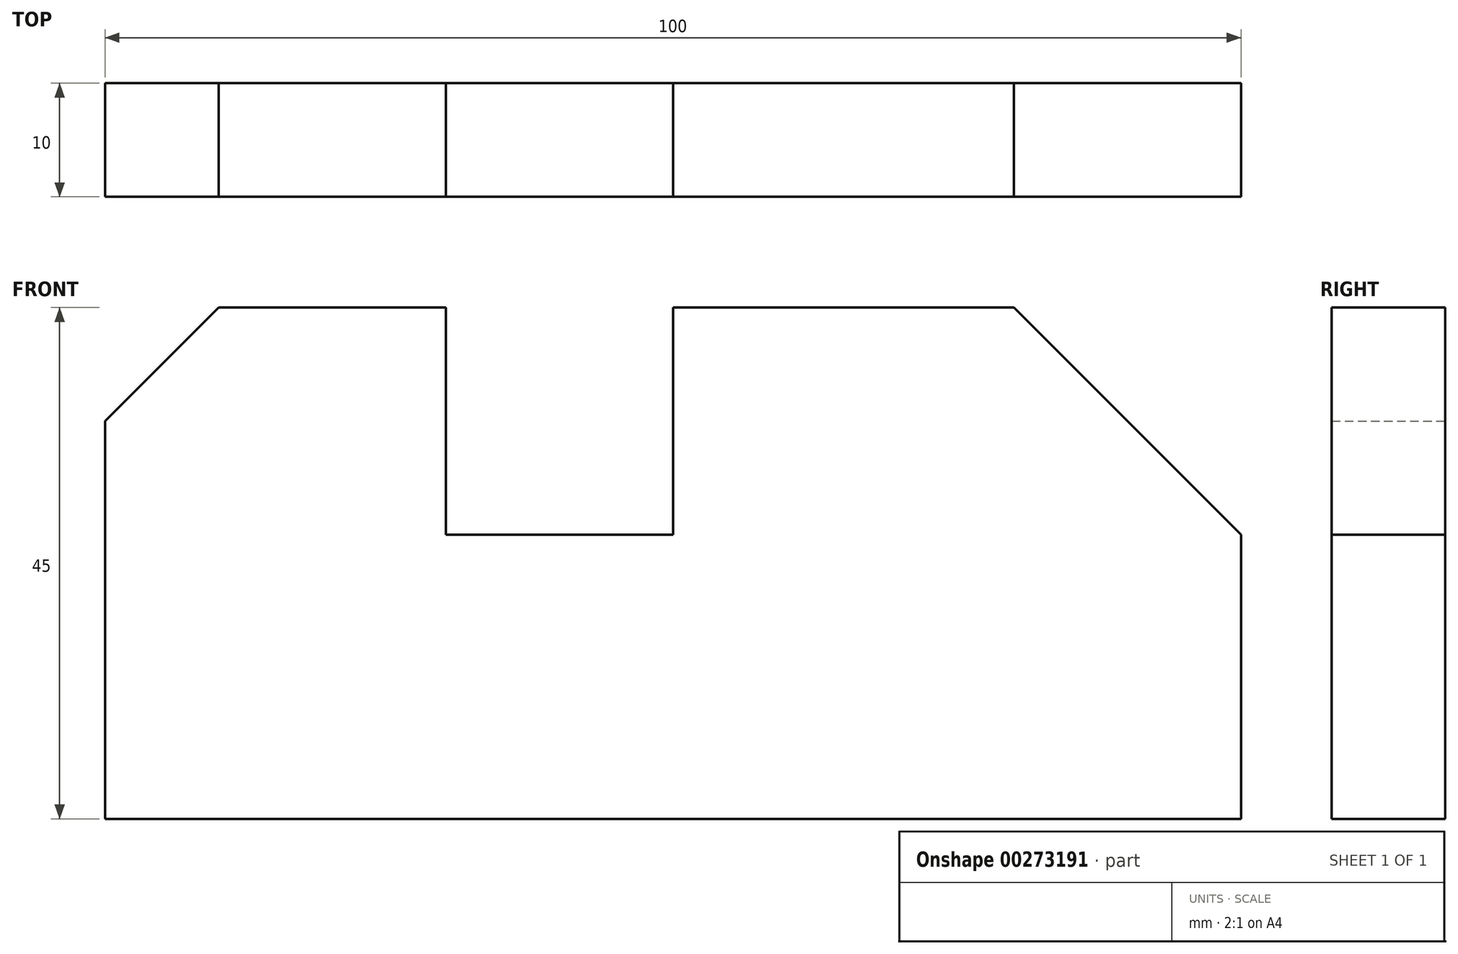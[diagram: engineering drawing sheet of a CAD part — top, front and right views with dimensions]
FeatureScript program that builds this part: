
annotation { "Feature Type Name" : "Feature", "Feature Type Description" : "" }
export const myFeature = defineFeature(function(context is Context, id is Id, definition is map)
    precondition{}
    {
        {
            var Q0;
            Q0=qCreatedBy(makeId("Front.planeOp"),FACE);
            var sketch = newSketch(context, id + "F0", { "sketchPlane" : qUnion([Q0])});
            skLineSegment(sketch, "E0", {"start": v(0, 0) * mm, "end": v(100, 0) * mm});
            skLineSegment(sketch, "E1", {"start": v(30, 45) * mm, "end": v(30, 25) * mm});
            skLineSegment(sketch, "E2", {"start": v(30, 25) * mm, "end": v(50, 25) * mm});
            skLineSegment(sketch, "E3", {"start": v(50, 25) * mm, "end": v(50, 45) * mm});
            skLineSegment(sketch, "E4", {"start": v(50, 45) * mm, "end": v(80, 45) * mm});
            skLineSegment(sketch, "E5", {"start": v(100, 0) * mm, "end": v(100, 25) * mm});
            skLineSegment(sketch, "E6", {"start": v(100, 25) * mm, "end": v(80, 45) * mm});
            skLineSegment(sketch, "E7", {"start": v(30, 45) * mm, "end": v(10, 45) * mm});
            skLineSegment(sketch, "E8", {"start": v(10, 45) * mm, "end": v(0, 35) * mm});
            skLineSegment(sketch, "E9", {"start": v(0, 35) * mm, "end": v(0, 0) * mm});
            skSolve(sketch);
        }
        {
            var Q0;
            Q0=makeQuery(id+"F0.imprint","IMPRINT",FACE,{"disambiguationData":[TD([[makeQuery(id+"F0.imprint","IMPRINT",EDGE,{"derivedFrom":sQuery(id+"F0.wireOp",EDGE,"E0")}),1.0]])]});
            extrude(context, id + "F1", {"entities" : qUnion([Q0]), "depth" : 10 * mm});
        }
    });
